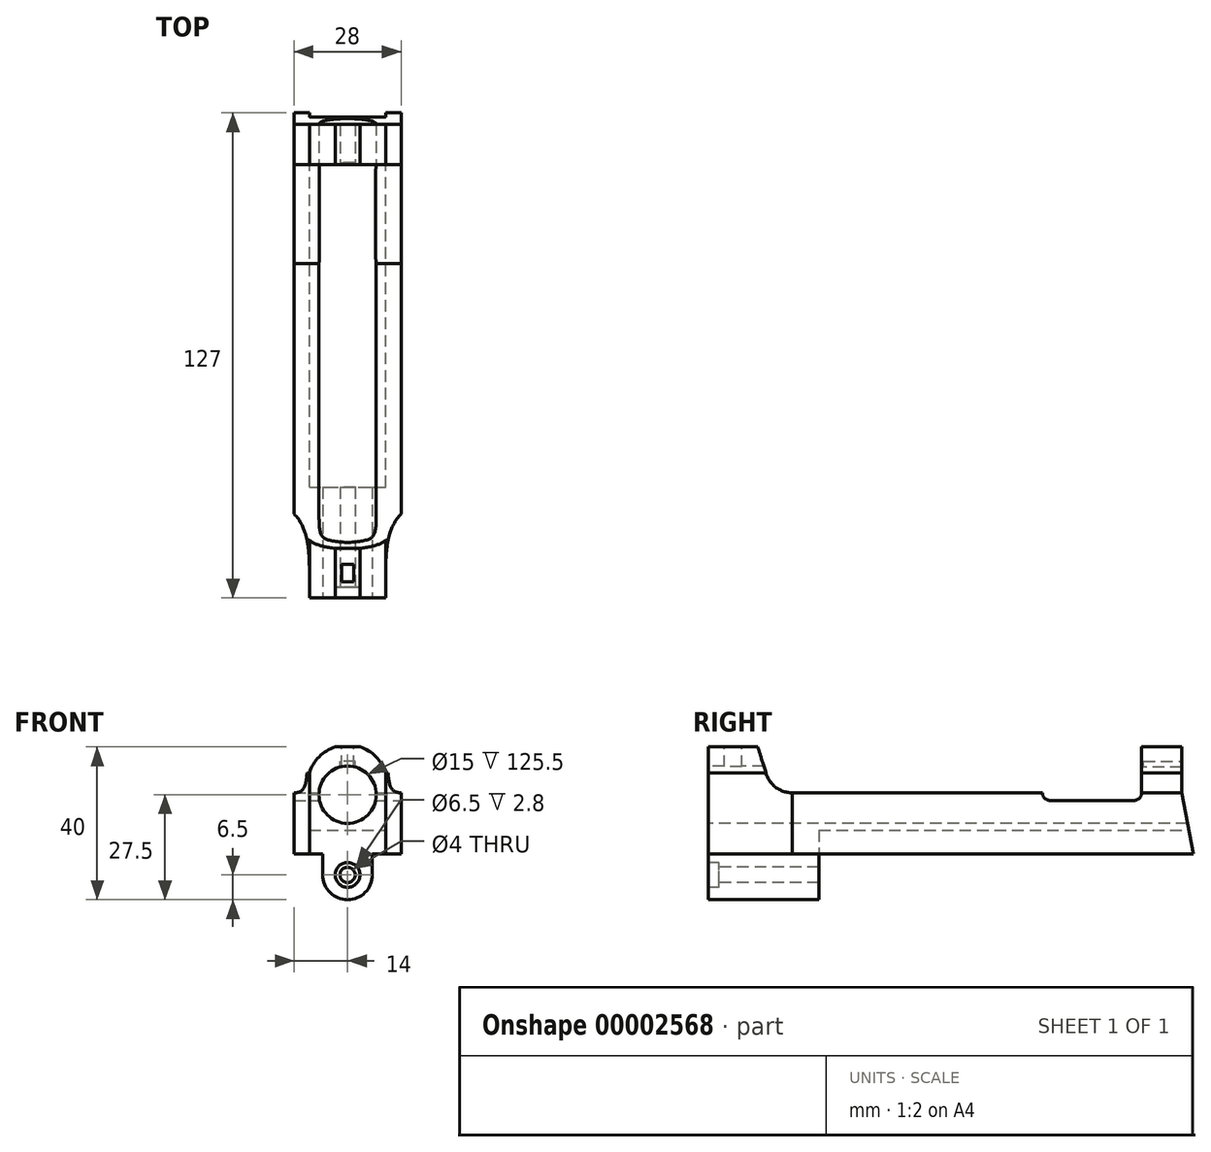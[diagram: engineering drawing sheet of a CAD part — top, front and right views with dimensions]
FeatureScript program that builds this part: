
annotation { "Feature Type Name" : "Feature", "Feature Type Description" : "" }
export const myFeature = defineFeature(function(context is Context, id is Id, definition is map)
    precondition{}
    {
        {
            var Q0;
            Q0=qCreatedBy(makeId("Front.planeOp"),FACE);
            var sketch = newSketch(context, id + "F0", { "sketchPlane" : qUnion([Q0])});
            skLineSegment(sketch, "E0.top", {"start": v(6.75, 40) * mm, "end": v(13.25, 40) * mm});
            skLineSegment(sketch, "E0.left", {"start": v(0, 28) * mm, "end": v(0, 33.25) * mm});
            skArc(sketch, "E1", {"start": v(20, 33.25) * mm, "mid": v(17.44, 37.44) * mm, "end": v(13.25, 40) * mm});
            skPoint(sketch, "E1.first.point", {"position": v(6.75, 40) * mm});
            skPoint(sketch, "E1.second.point", {"position": v(13.25, 40) * mm});
            skPoint(sketch, "E1.third.point", {"position": v(10, 19.49) * mm});
            skLineSegment(sketch, "E2", {"start": v(10, 0) * mm, "end": v(10, 40) * mm, "construction": true});
            skArc(sketch, "E3.trimOffspring", {"start": v(6.75, 40) * mm, "mid": v(2.56, 37.44) * mm, "end": v(0, 33.25) * mm});
            skPoint(sketch, "E4.orphan", {"position": v(0, 40) * mm});
            skPoint(sketch, "E5.orphan", {"position": v(20, 40) * mm});
            skCircle(sketch, "E6", {"center": v(10, 27.5) * mm, "radius": 7.5 * mm});
            skArc(sketch, "E7", {"start": v(3.5, 6.5) * mm, "mid": v(10, 0) * mm, "end": v(16.5, 6.5) * mm});
            skLineSegment(sketch, "E8", {"start": v(0, 12) * mm, "end": v(3.5, 12) * mm});
            skLineSegment(sketch, "E9", {"start": v(3.5, 12) * mm, "end": v(3.5, 6.5) * mm});
            skLineSegment(sketch, "E10", {"start": v(16.5, 12) * mm, "end": v(16.5, 6.5) * mm});
            skLineSegment(sketch, "E11.trimOffspring", {"start": v(16.5, 12) * mm, "end": v(20, 12) * mm});
            skPoint(sketch, "E12.orphan", {"position": v(0, 0) * mm});
            skPoint(sketch, "E13.orphan", {"position": v(20, 0) * mm});
            skLineSegment(sketch, "E14", {"start": v(-4, 28) * mm, "end": v(-4, 12) * mm});
            skLineSegment(sketch, "E15", {"start": v(0, 12) * mm, "end": v(-4, 12) * mm});
            skLineSegment(sketch, "E16", {"start": v(-4, 28) * mm, "end": v(0, 28) * mm});
            skLineSegment(sketch, "E17.0.MirrorCS", {"start": v(20, 12) * mm, "end": v(24, 12) * mm});
            skLineSegment(sketch, "E17.1.MirrorCS", {"start": v(24, 28) * mm, "end": v(24, 12) * mm});
            skLineSegment(sketch, "E17.2.MirrorCS", {"start": v(20, 28) * mm, "end": v(20, 33.25) * mm});
            skLineSegment(sketch, "E17.3.MirrorCS", {"start": v(24, 28) * mm, "end": v(20, 28) * mm});
            skSolve(sketch);
        }
        {
            var Q0;
            Q0=makeQuery(id+"F0.imprint","IMPRINT",FACE,{"disambiguationData":[TD([[makeQuery(id+"F0.imprint","IMPRINT",EDGE,{"derivedFrom":sQuery(id+"F0.wireOp",EDGE,"E0.top")}),-1.0]])]});
            extrude(context, id + "F1", {"entities" : qUnion([Q0]), "oppositeDirection" : true, "depth" : 127 * mm});
        }
        {
            var Q0;
            Q0=makeQuery(id+"F1.opExtrude","SWEPT_FACE",FACE,{"disambiguationData":[OSD([sQuery(id+"F0.wireOp",EDGE,"E0.left")])]});
            var sketch = newSketch(context, id + "F2", { "sketchPlane" : qUnion([Q0])});
            skLineSegment(sketch, "E18.bottom", {"start": v(0, 33.25) * mm, "end": v(-27.15, 33.25) * mm});
            skLineSegment(sketch, "E18.top", {"start": v(0, 28) * mm, "end": v(-27.15, 28) * mm});
            skLineSegment(sketch, "E18.left", {"start": v(0, 33.25) * mm, "end": v(0, 28) * mm});
            skLineSegment(sketch, "E18.right", {"start": v(-27.15, 33.25) * mm, "end": v(-27.15, 28) * mm});
            skSolve(sketch);
        }
        {
            var Q0;
            Q0=makeQuery(id+"F1.opExtrude","SWEPT_FACE",FACE,{"disambiguationData":[OSD([sQuery(id+"F0.wireOp",EDGE,"E17.2.MirrorCS")])]});
            var sketch = newSketch(context, id + "F3", { "sketchPlane" : qUnion([Q0])});
            skLineSegment(sketch, "E19.0", {"start": v(0, 33.25) * mm, "end": v(27.15, 33.25) * mm});
            skLineSegment(sketch, "E20.0", {"start": v(27.15, 33.25) * mm, "end": v(27.15, 28) * mm});
            skLineSegment(sketch, "E21.0", {"start": v(0, 28) * mm, "end": v(27.15, 28) * mm});
            skLineSegment(sketch, "E22.0", {"start": v(0, 33.25) * mm, "end": v(0, 28) * mm});
            skSolve(sketch);
        }
        {
            var Q0;
            Q0=makeQuery(id+"F2.imprint","IMPRINT",FACE,{"disambiguationData":[TD([[makeQuery(id+"F2.imprint","IMPRINT",EDGE,{"derivedFrom":sQuery(id+"F2.wireOp",EDGE,"E18.bottom")}),-1.0]])]});
            var Q1;
            Q1=makeQuery(id+"F1.opExtrude","SWEPT_FACE",FACE,{"disambiguationData":[OSD([sQuery(id+"F0.wireOp",EDGE,"E14")])]});
            extrude(context, id + "F4", {"entities" : qUnion([Q0]), "operationType" : NewBodyOperationType.ADD, "endBound" : BoundingType.UP_TO_SURFACE, "endBoundEntityFace" : qUnion([Q1]), "depth" : 25 * mm});
        }
        {
            var Q0;
            Q0=makeQuery(id+"F3.imprint","IMPRINT",FACE,{"disambiguationData":[TD([[makeQuery(id+"F3.imprint","IMPRINT",EDGE,{"derivedFrom":sQuery(id+"F3.wireOp",EDGE,"E19.0")}),1.0]])]});
            var Q1;
            Q1=makeQuery(id+"F1.opExtrude","SWEPT_FACE",FACE,{"disambiguationData":[OSD([sQuery(id+"F0.wireOp",EDGE,"E17.1.MirrorCS")])]});
            extrude(context, id + "F5", {"entities" : qUnion([Q0]), "operationType" : NewBodyOperationType.ADD, "endBound" : BoundingType.UP_TO_SURFACE, "endBoundEntityFace" : qUnion([Q1]), "depth" : 25 * mm});
        }
        {
            var Q0;
            {var subQ0=sQuery(id+"F0.wireOp",EDGE,"E17.1.MirrorCS");Q0=makeQuery(id+"F5.boolean.opBoolean","MERGE",FACE,{"derivedFrom":[makeQuery(id+"F1.opExtrude","SWEPT_FACE",FACE,{"disambiguationData":[OSD([subQ0])]}),makeQuery(id+"F5.opExtrude","CAP_FACE",FACE,{"disambiguationData":[OSD([subQ0])],"isStart":false})]});}
            var sketch = newSketch(context, id + "F6", { "sketchPlane" : qUnion([Q0])});
            skLineSegment(sketch, "E23.0", {"start": v(127, 40) * mm, "end": v(13, 40) * mm});
            skPoint(sketch, "E24", {"position": v(13, 40) * mm});
            skLineSegment(sketch, "E25.0", {"start": v(127, 28) * mm, "end": v(22, 28) * mm});
            skPoint(sketch, "E26", {"position": v(22, 28) * mm});
            skLineSegment(sketch, "E27", {"start": v(13, 40) * mm, "end": v(15.2, 33) * mm});
            skArc(sketch, "E28", {"start": v(15.2, 33) * mm, "mid": v(17.78, 29.38) * mm, "end": v(22, 28) * mm});
            skPoint(sketch, "E29", {"position": v(87.5, 28) * mm});
            skLineSegment(sketch, "E30", {"start": v(111.5, 26) * mm, "end": v(89.5, 26) * mm});
            skArc(sketch, "E31", {"start": v(89.5, 26) * mm, "mid": v(88.09, 26.59) * mm, "end": v(87.5, 28) * mm});
            skPoint(sketch, "E32", {"position": v(111.5, 26) * mm});
            skArc(sketch, "E33", {"start": v(111.5, 26) * mm, "mid": v(112.91, 26.59) * mm, "end": v(113.5, 28) * mm});
            skLineSegment(sketch, "E34", {"start": v(113.5, 28) * mm, "end": v(113.5, 40) * mm});
            skPoint(sketch, "E35", {"position": v(124, 40) * mm});
            skLineSegment(sketch, "E36", {"start": v(124, 40) * mm, "end": v(124, 28) * mm});
            skPoint(sketch, "E37", {"position": v(127, 12) * mm});
            skLineSegment(sketch, "E38", {"start": v(124, 28) * mm, "end": v(127, 12) * mm});
            skLineSegment(sketch, "E39", {"start": v(127, 12) * mm, "end": v(127, 40) * mm});
            skPoint(sketch, "E40.orphan", {"position": v(0, 40) * mm});
            skPoint(sketch, "E41.orphan", {"position": v(0, 28) * mm});
            skSolve(sketch);
        }
        {
            var Q0;
            {var subQ4=sQuery(id+"F6.wireOp",EDGE,"E28");Q0=makeQuery(id+"F6.imprint","IMPRINT",FACE,{"disambiguationData":[TD([[makeQuery(id+"F6.imprint","IMPRINT",EDGE,{"derivedFrom":subQ4}),1.0]])]});}
            var Q1;
            {var subQ5=sQuery(id+"F6.wireOp",EDGE,"E36");Q1=makeQuery(id+"F6.imprint","IMPRINT",FACE,{"disambiguationData":[TD([[makeQuery(id+"F6.imprint","IMPRINT",EDGE,{"derivedFrom":subQ5}),1.0]])]});}
            var Q2;
            {var subQ3=sQuery(id+"F6.wireOp",EDGE,"E38");Q2=makeQuery(id+"F6.imprint","IMPRINT",FACE,{"disambiguationData":[TD([[makeQuery(id+"F6.imprint","IMPRINT",EDGE,{"derivedFrom":subQ3}),1.0]])]});}
            var Q3;
            Q3=makeQuery(id+"F6.imprint","IMPRINT",FACE,{"disambiguationData":[TD([[makeQuery(id+"F6.imprint","IMPRINT",EDGE,{"derivedFrom":sQuery(id+"F6.wireOp",EDGE,"E30")}),-1.0]])]});
            var Q4;
            {var subQ1=sQuery(id+"F6.wireOp",EDGE,"E34");Q4=makeQuery(id+"F6.imprint","IMPRINT",FACE,{"disambiguationData":[TD([[makeQuery(id+"F6.imprint","IMPRINT",EDGE,{"derivedFrom":subQ1}),1.0]])]});}
            extrude(context, id + "F7", {"entities" : qUnion([Q0, Q1, Q2, Q3, Q4]), "operationType" : NewBodyOperationType.REMOVE, "endBound" : BoundingType.THROUGH_ALL, "oppositeDirection" : true, "depth" : 25 * mm});
        }
        {
            var Q0;
            {var subQ2=sQuery(id+"F0.wireOp",EDGE,"E0.top");Q0=makeQuery(id+"F7.boolean.opBoolean","SPLIT",FACE,{"disambiguationData":[TD([makeQuery(id+"F4.opExtrude","SWEPT_FACE",FACE,{"disambiguationData":[OSD([sQuery(id+"F2.wireOp",EDGE,"E18.left")])]})])],"derivedFrom":makeQuery(id+"F1.opExtrude","SWEPT_FACE",FACE,{"disambiguationData":[OSD([subQ2])]})});}
            var sketch = newSketch(context, id + "F8", { "sketchPlane" : qUnion([Q0])});
            skLineSegment(sketch, "E42", {"start": v(10, 0) * mm, "end": v(10, 13) * mm, "construction": true});
            skLineSegment(sketch, "E43.rect.bottom", {"start": v(11.6, 4.25) * mm, "end": v(8.4, 4.25) * mm});
            skLineSegment(sketch, "E43.rect.top", {"start": v(11.6, 8.75) * mm, "end": v(8.4, 8.75) * mm});
            skLineSegment(sketch, "E43.rect.left", {"start": v(11.6, 4.25) * mm, "end": v(11.6, 8.75) * mm});
            skLineSegment(sketch, "E43.rect.right", {"start": v(8.4, 4.25) * mm, "end": v(8.4, 8.75) * mm});
            skPoint(sketch, "E43.rect.middle", {"position": v(10, 6.5) * mm});
            skSolve(sketch);
        }
        {
            var Q0;
            Q0=makeQuery(id+"F8.imprint","IMPRINT",FACE,{"disambiguationData":[TD([[makeQuery(id+"F8.imprint","IMPRINT",EDGE,{"derivedFrom":sQuery(id+"F8.wireOp",EDGE,"E43.rect.bottom")}),-1.0]])]});
            extrude(context, id + "F9", {"entities" : qUnion([Q0]), "operationType" : NewBodyOperationType.REMOVE, "endBound" : BoundingType.UP_TO_NEXT, "oppositeDirection" : true, "depth" : 25 * mm});
        }
        {
            var Q0;
            Q0=makeQuery(id+"F1.opExtrude","SWEPT_FACE",FACE,{"disambiguationData":[OSD([sQuery(id+"F0.wireOp",EDGE,"E10")])]});
            var sketch = newSketch(context, id + "F10", { "sketchPlane" : qUnion([Q0])});
            skLineSegment(sketch, "E44.bottom", {"start": v(29, 12) * mm, "end": v(127, 12) * mm});
            skLineSegment(sketch, "E44.top", {"start": v(29, 0) * mm, "end": v(127, 0) * mm});
            skLineSegment(sketch, "E44.left", {"start": v(29, 12) * mm, "end": v(29, 0) * mm});
            skLineSegment(sketch, "E44.right", {"start": v(127, 12) * mm, "end": v(127, 0) * mm});
            skSolve(sketch);
        }
        {
            var Q0;
            {var subQ7=sQuery(id+"F10.wireOp",EDGE,"E44.top");var subQ8=sQuery(id+"F10.wireOp",EDGE,"E44.bottom");Q0=qUnion([makeQuery(id+"F10.imprint","IMPRINT",FACE,{"disambiguationData":[TD([[makeQuery(id+"F10.imprint","IMPRINT",EDGE,{"derivedFrom":subQ7}),1.0]])]}),makeQuery(id+"F10.imprint","IMPRINT",FACE,{"disambiguationData":[TD([[makeQuery(id+"F10.imprint","IMPRINT",EDGE,{"derivedFrom":subQ8}),1.0]])]})]);}
            extrude(context, id + "F11", {"entities" : qUnion([Q0]), "operationType" : NewBodyOperationType.REMOVE, "endBound" : BoundingType.THROUGH_ALL, "oppositeDirection" : true, "depth" : 25 * mm});
        }
        {
            var Q0;
            Q0=makeQuery(id+"F5.boolean.opBoolean","MERGE",FACE,{"derivedFrom":[makeQuery(id+"F4.boolean.opBoolean","MERGE",FACE,{"derivedFrom":[makeQuery(id+"F1.opExtrude","CAP_FACE",FACE,{"disambiguationData":[OSD([sQuery(id+"F0.wireOp",EDGE,"E0.top"),sQuery(id+"F0.wireOp",EDGE,"E0.left"),sQuery(id+"F0.wireOp",EDGE,"E1"),sQuery(id+"F0.wireOp",EDGE,"E3.trimOffspring"),sQuery(id+"F0.wireOp",EDGE,"E6"),sQuery(id+"F0.wireOp",EDGE,"E7"),sQuery(id+"F0.wireOp",EDGE,"E9"),sQuery(id+"F0.wireOp",EDGE,"E10"),sQuery(id+"F0.wireOp",EDGE,"E11.trimOffspring"),sQuery(id+"F0.wireOp",EDGE,"E14"),sQuery(id+"F0.wireOp",EDGE,"E15"),sQuery(id+"F0.wireOp",EDGE,"E16"),sQuery(id+"F0.wireOp",EDGE,"E17.1.MirrorCS"),sQuery(id+"F0.wireOp",EDGE,"E17.2.MirrorCS"),sQuery(id+"F0.wireOp",EDGE,"E17.3.MirrorCS")])],"isStart":true}),makeQuery(id+"F4.opExtrude","SWEPT_FACE",FACE,{"disambiguationData":[OSD([sQuery(id+"F2.wireOp",EDGE,"E18.left")])]})]}),makeQuery(id+"F5.opExtrude","SWEPT_FACE",FACE,{"disambiguationData":[OSD([sQuery(id+"F3.wireOp",EDGE,"E22.0")])]})]});
            var sketch = newSketch(context, id + "F12", { "sketchPlane" : qUnion([Q0])});
            skCircle(sketch, "E45", {"center": v(10, 6.5) * mm, "radius": 3.25 * mm});
            skSolve(sketch);
        }
        {
            var Q0;
            Q0=makeQuery(id+"F12.imprint","IMPRINT",FACE,{"disambiguationData":[TD([[makeQuery(id+"F12.imprint","IMPRINT",EDGE,{"derivedFrom":sQuery(id+"F12.wireOp",EDGE,"E45")}),1.0]])]});
            extrude(context, id + "F13", {"entities" : qUnion([Q0]), "operationType" : NewBodyOperationType.REMOVE, "oppositeDirection" : true, "depth" : 2.8 * mm});
        }
        {
            var Q0;
            Q0=makeQuery(id+"F13.boolean.opBoolean","COPY",FACE,{"derivedFrom":makeQuery(id+"F13.opExtrude","CAP_FACE",FACE,{"disambiguationData":[OSD([sQuery(id+"F12.wireOp",EDGE,"E45")])],"isStart":false})});
            var sketch = newSketch(context, id + "F14", { "sketchPlane" : qUnion([Q0])});
            skCircle(sketch, "E46", {"center": v(10, 6.5) * mm, "radius": 2 * mm});
            skSolve(sketch);
        }
        {
            var Q0;
            Q0=makeQuery(id+"F14.imprint","IMPRINT",FACE,{"disambiguationData":[TD([[makeQuery(id+"F14.imprint","IMPRINT",EDGE,{"derivedFrom":sQuery(id+"F14.wireOp",EDGE,"E46")}),1.0]])]});
            extrude(context, id + "F15", {"entities" : qUnion([Q0]), "operationType" : NewBodyOperationType.REMOVE, "endBound" : BoundingType.THROUGH_ALL, "oppositeDirection" : true, "depth" : 25 * mm});
        }
        {
            var Q0;
            Q0=makeQuery(id+"F7.boolean.opBoolean","COPY",FACE,{"derivedFrom":makeQuery(id+"F7.opExtrude","SWEPT_FACE",FACE,{"disambiguationData":[OSD([sQuery(id+"F6.wireOp",EDGE,"E36")])]})});
            var sketch = newSketch(context, id + "F16", { "sketchPlane" : qUnion([Q0])});
            skLineSegment(sketch, "E47.rect.bottom", {"start": v(-12, 33.8) * mm, "end": v(-8, 33.8) * mm});
            skLineSegment(sketch, "E47.rect.top", {"start": v(-12, 36.2) * mm, "end": v(-8, 36.2) * mm});
            skLineSegment(sketch, "E47.rect.left", {"start": v(-12, 33.8) * mm, "end": v(-12, 36.2) * mm});
            skLineSegment(sketch, "E47.rect.right", {"start": v(-8, 33.8) * mm, "end": v(-8, 36.2) * mm});
            skPoint(sketch, "E47.rect.middle", {"position": v(-10, 35) * mm});
            skSolve(sketch);
        }
        {
            var Q0;
            {var subQ5=sQuery(id+"F16.wireOp",EDGE,"E47.rect.bottom");Q0=makeQuery(id+"F16.imprint","IMPRINT",FACE,{"disambiguationData":[TD([[makeQuery(id+"F16.imprint","IMPRINT",EDGE,{"derivedFrom":subQ5}),1.0]])]});}
            var Q1;
            {var subQ5=sQuery(id+"F16.wireOp",EDGE,"E47.rect.top");Q1=makeQuery(id+"F16.imprint","IMPRINT",FACE,{"disambiguationData":[TD([[makeQuery(id+"F16.imprint","IMPRINT",EDGE,{"derivedFrom":subQ5}),-1.0]])]});}
            extrude(context, id + "F17", {"entities" : qUnion([Q0, Q1]), "operationType" : NewBodyOperationType.REMOVE, "oppositeDirection" : true, "depth" : 10 * mm});
        }
        {
            var Q0;
            Q0=qCreatedBy(makeId("Top.planeOp"),FACE);
            var sketch = newSketch(context, id + "F18", { "sketchPlane" : qUnion([Q0])});
            skLineSegment(sketch, "E48", {"start": v(24, 0) * mm, "end": v(20, 0) * mm});
            skPoint(sketch, "E49", {"position": v(20, 7) * mm});
            skFitSpline(sketch, "E50", {"points": [v(20, 7) * mm, v(24, 22) * mm], "startDerivative": vector(0, 16.3) * mm, "endDerivative": vector(11.26, 11.71) * mm});
            skLineSegment(sketch, "E51.trimOffspring", {"start": v(20, 7) * mm, "end": v(20, 0) * mm});
            skLineSegment(sketch, "E52", {"start": v(24, 0) * mm, "end": v(24, 22) * mm});
            skLineSegment(sketch, "E53", {"start": v(10, 6.5) * mm, "end": v(10, 1.44) * mm, "construction": true});
            skLineSegment(sketch, "E54.0.MirrorCS", {"start": v(0, 7) * mm, "end": v(0, 0) * mm});
            skFitSpline(sketch, "E55.0.MirrorCS", {"points": [v(0, 7) * mm, v(-4, 22) * mm], "startDerivative": vector(0, 16.3) * mm, "endDerivative": vector(-11.26, 11.71) * mm});
            skLineSegment(sketch, "E56.0.MirrorCS", {"start": v(-4, 0) * mm, "end": v(-4, 22) * mm});
            skLineSegment(sketch, "E57.0.MirrorCS", {"start": v(-4, 0) * mm, "end": v(0, 0) * mm});
            skSolve(sketch);
        }
        {
            var Q0;
            {Q0=qUnion([makeQuery(id+"F18.imprint","IMPRINT",FACE,{"disambiguationData":[TD([[makeQuery(id+"F18.imprint","IMPRINT",EDGE,{"derivedFrom":sQuery(id+"F18.wireOp",EDGE,"E48")}),-1.0]])]}),makeQuery(id+"F18.imprint","IMPRINT",FACE,{"disambiguationData":[TD([[makeQuery(id+"F18.imprint","IMPRINT",EDGE,{"derivedFrom":sQuery(id+"F18.wireOp",EDGE,"E54.0.MirrorCS")}),-1.0]])]})]);}
            extrude(context, id + "F19", {"entities" : qUnion([Q0]), "operationType" : NewBodyOperationType.REMOVE, "endBound" : BoundingType.THROUGH_ALL, "depth" : 25 * mm});
        }
        {
            var Q0;
            Q0=makeQuery(id+"F11.boolean.opBoolean","MERGE",FACE,{"derivedFrom":[makeQuery(id+"F1.opExtrude","SWEPT_FACE",FACE,{"disambiguationData":[OSD([sQuery(id+"F0.wireOp",EDGE,"E11.trimOffspring")])]}),makeQuery(id+"F1.opExtrude","SWEPT_FACE",FACE,{"disambiguationData":[OSD([sQuery(id+"F0.wireOp",EDGE,"E15")])]}),makeQuery(id+"F11.opExtrude","SWEPT_FACE",FACE,{"disambiguationData":[OSD([sQuery(id+"F10.wireOp",EDGE,"E44.bottom")])]})]});
            var sketch = newSketch(context, id + "F20", { "sketchPlane" : qUnion([Q0])});
            skLineSegment(sketch, "E58.bottom", {"start": v(0, -29) * mm, "end": v(20, -29) * mm});
            skLineSegment(sketch, "E58.top", {"start": v(0, -127) * mm, "end": v(20, -127) * mm});
            skLineSegment(sketch, "E58.left", {"start": v(0, -29) * mm, "end": v(0, -127) * mm});
            skLineSegment(sketch, "E58.right", {"start": v(20, -29) * mm, "end": v(20, -127) * mm});
            skSolve(sketch);
        }
        {
            var Q0;
            Q0=makeQuery(id+"F20.imprint","IMPRINT",FACE,{"disambiguationData":[TD([[makeQuery(id+"F20.imprint","IMPRINT",EDGE,{"derivedFrom":sQuery(id+"F20.wireOp",EDGE,"E58.top")}),-1.0]])]});
            extrude(context, id + "F21", {"entities" : qUnion([Q0]), "operationType" : NewBodyOperationType.REMOVE, "oppositeDirection" : true, "depth" : 6.2 * mm});
        }
    });
